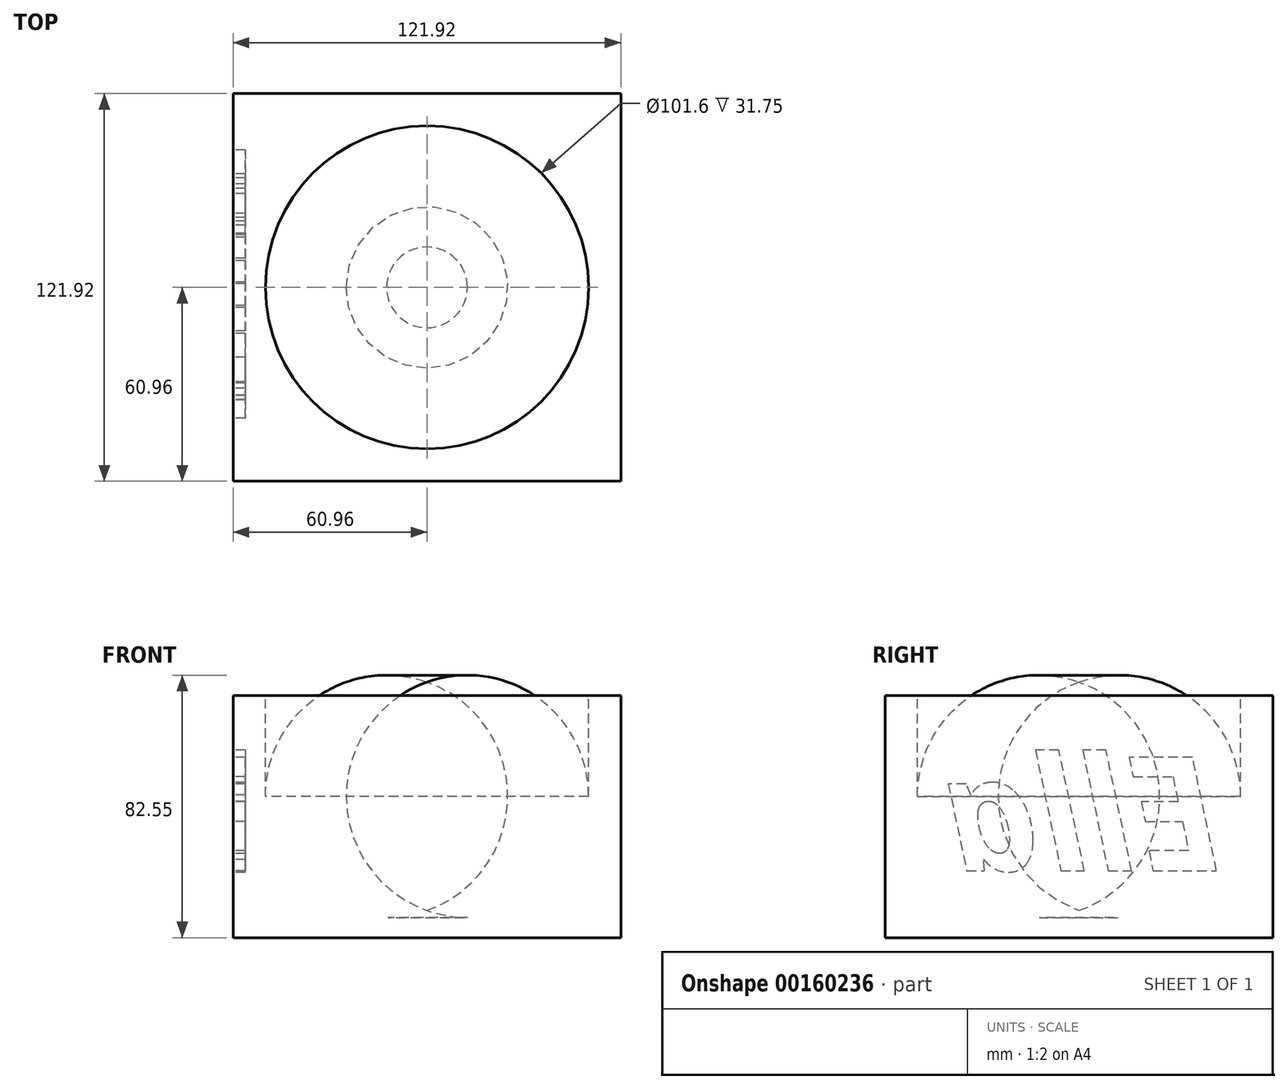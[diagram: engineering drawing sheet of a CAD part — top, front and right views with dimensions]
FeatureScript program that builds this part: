
annotation { "Feature Type Name" : "Feature", "Feature Type Description" : "" }
export const myFeature = defineFeature(function(context is Context, id is Id, definition is map)
    precondition{}
    {
        {
            var Q0;
            Q0=qCreatedBy(makeId("Top.planeOp"),FACE);
            var sketch = newSketch(context, id + "F0", { "sketchPlane" : qUnion([Q0])});
            skLineSegment(sketch, "E0.bottom", {"start": v(-60.96, 60.96) * mm, "end": v(60.96, 60.96) * mm});
            skLineSegment(sketch, "E0.top", {"start": v(-60.96, -60.96) * mm, "end": v(60.96, -60.96) * mm});
            skLineSegment(sketch, "E0.left", {"start": v(-60.96, 60.96) * mm, "end": v(-60.96, -60.96) * mm});
            skLineSegment(sketch, "E0.right", {"start": v(60.96, 60.96) * mm, "end": v(60.96, -60.96) * mm});
            skLineSegment(sketch, "E1", {"start": v(0, 60.96) * mm, "end": v(0, -60.96) * mm, "construction": true});
            skLineSegment(sketch, "E2", {"start": v(-60.96, 0) * mm, "end": v(60.96, 0) * mm, "construction": true});
            skSolve(sketch);
        }
        {
            var Q0;
            Q0 = qSketchRegion(id + "F0", true);
            extrude(context, id + "F1", {"entities" : qUnion([Q0]), "depth" : 76.2 * mm});
        }
        {
            var Q0;
            Q0=makeQuery(id+"F1.opExtrude","CAP_FACE",FACE,{"disambiguationData":[OSD([sQuery(id+"F0.wireOp",EDGE,"E0.bottom"),sQuery(id+"F0.wireOp",EDGE,"E0.top"),sQuery(id+"F0.wireOp",EDGE,"E0.left"),sQuery(id+"F0.wireOp",EDGE,"E0.right")])],"isStart":false});
            var sketch = newSketch(context, id + "F2", { "sketchPlane" : qUnion([Q0])});
            skCircle(sketch, "E3", {"center": v(0, 0) * mm, "radius": 50.8 * mm});
            skSolve(sketch);
        }
        {
            var Q0;
            Q0=makeQuery(id+"F2.imprint","IMPRINT",FACE,{"disambiguationData":[TD([[makeQuery(id+"F2.imprint","IMPRINT",EDGE,{"derivedFrom":sQuery(id+"F2.wireOp",EDGE,"E3")}),1.0]])]});
            var Q1;
            Q1=sQuery(id+"F2.wireOp",EDGE,"E3");
            extrude(context, id + "F3", {"entities" : qUnion([Q0]), "operationType" : NewBodyOperationType.REMOVE, "surfaceEntities" : qUnion([Q1]), "oppositeDirection" : true, "depth" : 69.85 * mm});
        }
        {
            var Q0;
            Q0=makeQuery(id+"F3.boolean.opBoolean","COPY",EDGE,{"derivedFrom":makeQuery(id+"F3.opExtrude","CAP_EDGE",EDGE,{"disambiguationData":[OSD([sQuery(id+"F2.wireOp",EDGE,"E3")])],"isStart":false})});
            fillet(context, id + "F4", {"entities" : qUnion([Q0]), "radius" : 38.1 * mm, "tangentPropagation" : true, "allowEdgeOverflow" : false});
        }
        {
            var Q0;
            Q0=makeQuery(id+"F1.opExtrude","SWEPT_FACE",FACE,{"disambiguationData":[OSD([sQuery(id+"F0.wireOp",EDGE,"E0.left")])]});
            var sketch = newSketch(context, id + "F5", { "sketchPlane" : qUnion([Q0])});
            skText(sketch, "E4", { "text": "Ella", "fontName": "OpenSans-BoldItalic.ttf"});
            const initialGuessF5  = {"E4": [-0.04454, 0.02107, 1, 0, 0.036]};
            skSetInitialGuess(sketch, initialGuessF5);
            skSolve(sketch);
        }
        {
            var Q0;
            Q0 = qSketchRegion(id + "F5", true);
            extrude(context, id + "F6", {"entities" : qUnion([Q0]), "operationType" : NewBodyOperationType.REMOVE, "oppositeDirection" : true, "depth" : 3.8 * mm});
        }
    });
